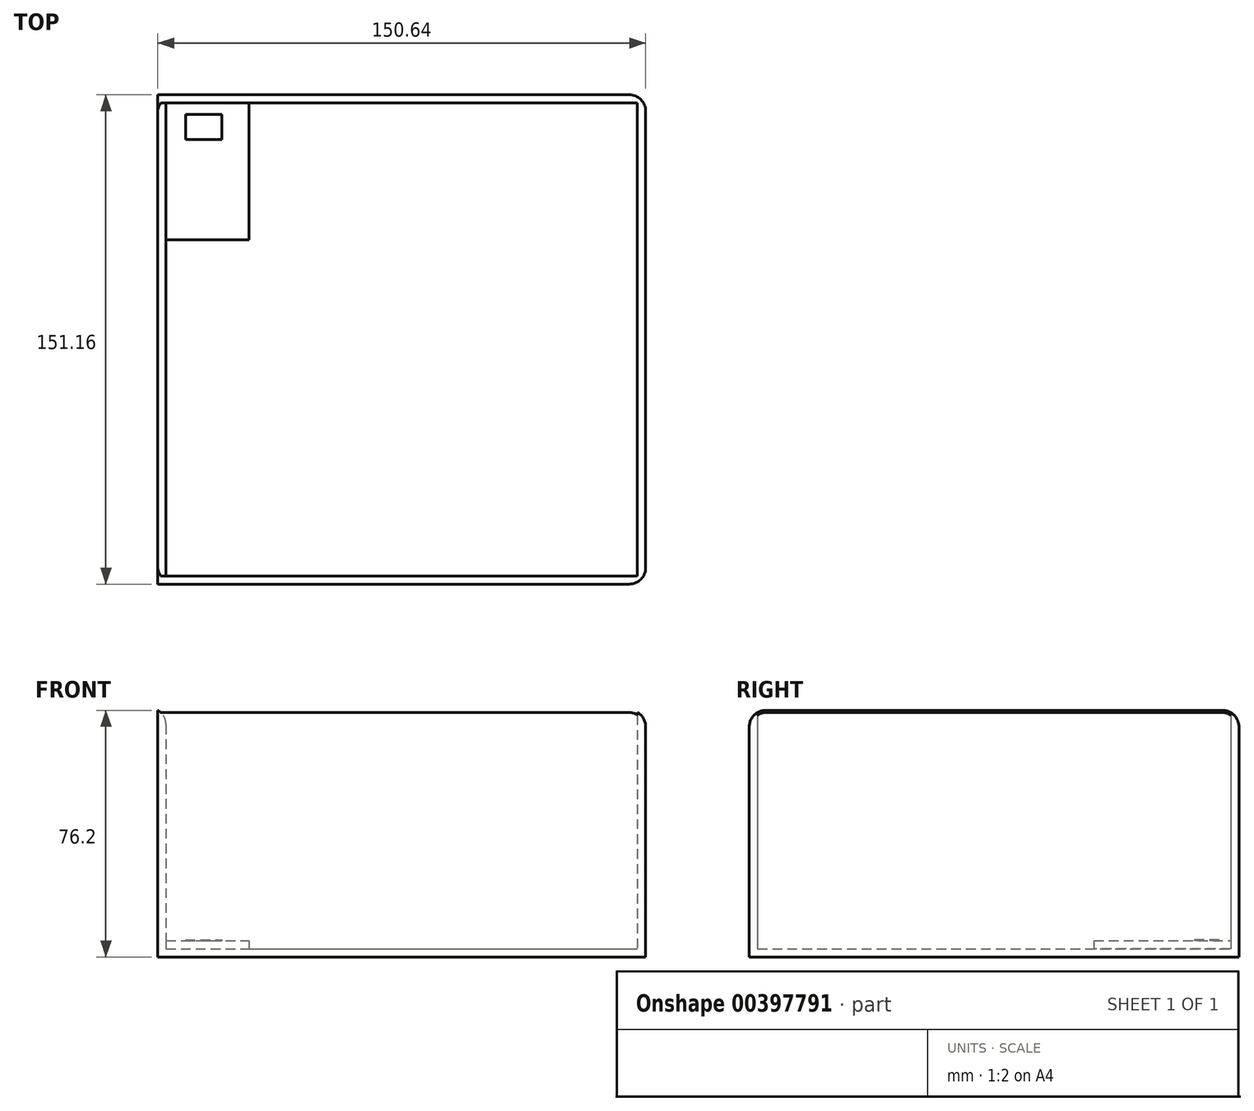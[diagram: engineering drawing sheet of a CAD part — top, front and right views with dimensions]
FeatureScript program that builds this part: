
annotation { "Feature Type Name" : "Feature", "Feature Type Description" : "" }
export const myFeature = defineFeature(function(context is Context, id is Id, definition is map)
    precondition{}
    {
        {
            var Q0;
            Q0=qCreatedBy(makeId("Top.planeOp"),FACE);
            var sketch = newSketch(context, id + "F0", { "sketchPlane" : qUnion([Q0])});
            skLineSegment(sketch, "E0.bottom", {"start": v(-75.44, -75.65) * mm, "end": v(75.2, -75.65) * mm});
            skLineSegment(sketch, "E0.top", {"start": v(-75.44, 75.51) * mm, "end": v(75.2, 75.51) * mm});
            skLineSegment(sketch, "E0.left", {"start": v(-75.44, -75.65) * mm, "end": v(-75.44, 75.51) * mm});
            skLineSegment(sketch, "E0.right", {"start": v(75.2, -75.65) * mm, "end": v(75.2, 75.51) * mm});
            skSolve(sketch);
        }
        {
            var Q0;
            Q0=makeQuery(id+"F0.imprint","IMPRINT",FACE,{"disambiguationData":[TD([[makeQuery(id+"F0.imprint","IMPRINT",EDGE,{"derivedFrom":sQuery(id+"F0.wireOp",EDGE,"E0.bottom")}),1.0]])]});
            extrude(context, id + "F1", {"entities" : qUnion([Q0]), "depth" : 76.2 * mm});
        }
        {
            var Q0;
            Q0=makeQuery(id+"F1.opExtrude","CAP_FACE",FACE,{"disambiguationData":[OSD([sQuery(id+"F0.wireOp",EDGE,"E0.bottom"),sQuery(id+"F0.wireOp",EDGE,"E0.top"),sQuery(id+"F0.wireOp",EDGE,"E0.left"),sQuery(id+"F0.wireOp",EDGE,"E0.right")])],"isStart":false});
            shell(context, id + "F2", {"entities" : qUnion([Q0]), "thickness" : 2.54 * mm});
        }
        {
            var Q0;
            Q0=makeQuery(id+"F1.opExtrude","CAP_EDGE",EDGE,{"disambiguationData":[OSD([sQuery(id+"F0.wireOp",EDGE,"E0.top")])],"isStart":false});
            fillet(context, id + "F3", {"entities" : qUnion([Q0]), "radius" : 5.08 * mm, "tangentPropagation" : true, "allowEdgeOverflow" : false});
        }
        {
            var Q0;
            Q0=makeQuery(id+"F1.opExtrude","CAP_EDGE",EDGE,{"disambiguationData":[OSD([sQuery(id+"F0.wireOp",EDGE,"E0.right")])],"isStart":false});
            fillet(context, id + "F4", {"entities" : qUnion([Q0]), "radius" : 5.08 * mm, "tangentPropagation" : true, "allowEdgeOverflow" : false});
        }
        {
            var Q0;
            Q0=makeQuery(id+"F1.opExtrude","CAP_EDGE",EDGE,{"disambiguationData":[OSD([sQuery(id+"F0.wireOp",EDGE,"E0.bottom")])],"isStart":false});
            fillet(context, id + "F5", {"entities" : qUnion([Q0]), "radius" : 5.08 * mm, "tangentPropagation" : true, "allowEdgeOverflow" : false});
        }
        {
            var Q0;
            {var subQ0=sQuery(id+"F0.wireOp",EDGE,"E0.left");Q0=makeQuery(id+"F2.opShell","OFFSET_EDGE",EDGE,{"disambiguationData":[OSD([subQ0]),TDD([makeQuery(id+"F1.opExtrude","CAP_EDGE",EDGE,{"disambiguationData":[OSD([subQ0])],"isStart":false})])]});}
            fillet(context, id + "F6", {"entities" : qUnion([Q0]), "radius" : 5.08 * mm, "tangentPropagation" : true, "allowEdgeOverflow" : false});
        }
        {
            var Q0;
            Q0=makeQuery(id+"F2.opShell","OFFSET_FACE",FACE,{"disambiguationData":[OSD([sQuery(id+"F0.wireOp",EDGE,"E0.bottom"),sQuery(id+"F0.wireOp",EDGE,"E0.top"),sQuery(id+"F0.wireOp",EDGE,"E0.left"),sQuery(id+"F0.wireOp",EDGE,"E0.right")])]});
            var sketch = newSketch(context, id + "F7", { "sketchPlane" : qUnion([Q0])});
            skLineSegment(sketch, "E1.bottom", {"start": v(-72.9, 72.97) * mm, "end": v(-47.23, 72.97) * mm});
            skLineSegment(sketch, "E1.top", {"start": v(-72.9, 30.73) * mm, "end": v(-47.23, 30.73) * mm});
            skLineSegment(sketch, "E1.left", {"start": v(-72.9, 72.97) * mm, "end": v(-72.9, 30.73) * mm});
            skLineSegment(sketch, "E1.right", {"start": v(-47.23, 72.97) * mm, "end": v(-47.23, 30.73) * mm});
            skSolve(sketch);
        }
        {
            var Q0;
            Q0=makeQuery(id+"F7.imprint","IMPRINT",FACE,{"disambiguationData":[TD([[makeQuery(id+"F7.imprint","IMPRINT",EDGE,{"derivedFrom":sQuery(id+"F7.wireOp",EDGE,"E1.bottom")}),-1.0]])]});
            extrude(context, id + "F8", {"entities" : qUnion([Q0]), "operationType" : NewBodyOperationType.ADD, "depth" : 2.54 * mm});
        }
        {
            var Q0;
            Q0=makeQuery(id+"F8.opExtrude","CAP_FACE",FACE,{"disambiguationData":[OSD([sQuery(id+"F7.wireOp",EDGE,"E1.bottom"),sQuery(id+"F7.wireOp",EDGE,"E1.top"),sQuery(id+"F7.wireOp",EDGE,"E1.left"),sQuery(id+"F7.wireOp",EDGE,"E1.right")])],"isStart":false});
            var sketch = newSketch(context, id + "F9", { "sketchPlane" : qUnion([Q0])});
            skLineSegment(sketch, "E2.bottom", {"start": v(-66.86, 69.39) * mm, "end": v(-55.6, 69.39) * mm});
            skLineSegment(sketch, "E2.top", {"start": v(-66.86, 61.74) * mm, "end": v(-55.6, 61.74) * mm});
            skLineSegment(sketch, "E2.left", {"start": v(-66.86, 69.39) * mm, "end": v(-66.86, 61.74) * mm});
            skLineSegment(sketch, "E2.right", {"start": v(-55.6, 69.39) * mm, "end": v(-55.6, 61.74) * mm});
            skSolve(sketch);
        }
        {
            var Q0;
            Q0=makeQuery(id+"F9.imprint","IMPRINT",FACE,{"disambiguationData":[TD([[makeQuery(id+"F9.imprint","IMPRINT",EDGE,{"derivedFrom":sQuery(id+"F9.wireOp",EDGE,"E2.bottom")}),-1.0]])]});
            extrude(context, id + "F10", {"entities" : qUnion([Q0]), "operationType" : NewBodyOperationType.ADD, "depth" : 0.25 * mm});
        }
    });
